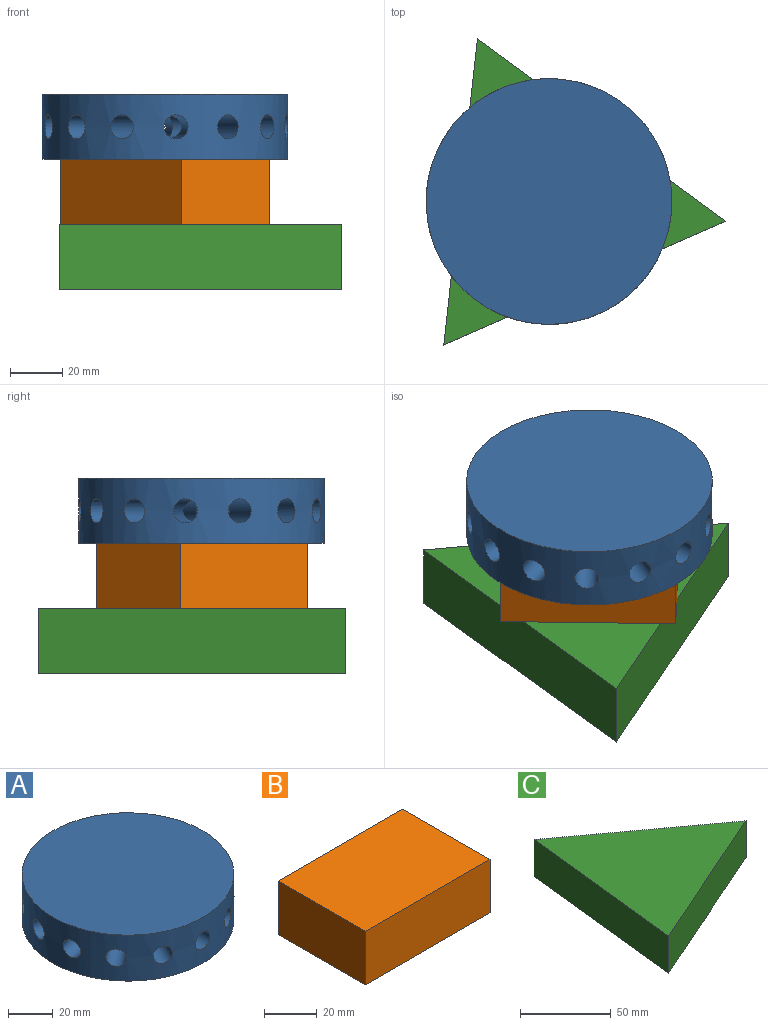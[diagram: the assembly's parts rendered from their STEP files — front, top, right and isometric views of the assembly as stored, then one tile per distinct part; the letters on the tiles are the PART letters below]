
ASSEMBLY  parts=3 mates=2
PART A: 17 faces, bbox 94.3x94.3x25 mm
  f0: cylinder r=47.14mm len=94.27mm, axis (0,0,-1), area 6466.9mm2, adj f1,f2,f3,f4,f5,f6,f7,f8
  f1: cylinder r=4.61mm len=48.01mm, axis (0.97,-0.22,0), area 989.8mm2, adj f0,f14,f15
  f2: cylinder r=4.61mm len=48.01mm, axis (0.97,-0.22,0), area 989.8mm2, adj f0,f13,f16
  f3: cylinder r=4.61mm len=46.47mm, axis (0.43,-0.9,0), area 989.8mm2, adj f0,f8,f16
  f4: cylinder r=4.61mm len=46.47mm, axis (0.43,-0.9,0), area 989.8mm2, adj f0,f7,f15
  f5: cylinder r=4.61mm len=42.6mm, axis (0.78,0.62,0), area 989.8mm2, adj f0,f12,f13
  f6: cylinder r=4.61mm len=42.6mm, axis (0.78,0.62,0), area 989.8mm2, adj f0,f11,f14
  f7: cylinder r=4.61mm len=47.14mm, axis (0,1,0), area 989.8mm2, adj f0,f4,f12
  f8: cylinder r=4.61mm len=47.14mm, axis (0,1,0), area 989.8mm2, adj f0,f3,f11
  f9: plane 94.27x94.27mm, normal (0,0,1), area 6979.8mm2, adj f0
  f10: plane 94.27x94.27mm, normal (0,0,-1), area 6979.8mm2, adj f0
  f11: cylinder r=4.61mm len=46.47mm, axis (-0.43,-0.9,0), area 989.8mm2, adj f0,f6,f8
  f12: cylinder r=4.61mm len=46.47mm, axis (-0.43,-0.9,0), area 989.8mm2, adj f0,f5,f7
  f13: cylinder r=4.61mm len=48.01mm, axis (-0.97,-0.22,0), area 989.8mm2, adj f0,f2,f5
  f14: cylinder r=4.61mm len=48.01mm, axis (-0.97,-0.22,0), area 989.8mm2, adj f0,f1,f6
  f15: cylinder r=4.61mm len=42.6mm, axis (-0.78,0.62,0), area 989.8mm2, adj f0,f1,f4
  f16: cylinder r=4.61mm len=42.6mm, axis (-0.78,0.62,0), area 989.8mm2, adj f0,f2,f3
PART B: 6 faces, bbox 67.2x47x25 mm
  f0: plane 67.23x25mm, normal (0,-1,0), area 1680.8mm2, adj f1,f3,f4,f5
  f1: plane 46.99x25mm, normal (1,0,0), area 1174.7mm2, adj f0,f2,f4,f5
  f2: plane 67.23x25mm, normal (0,1,0), area 1680.8mm2, adj f1,f3,f4,f5
  f3: plane 46.99x25mm, normal (-1,0,0), area 1174.7mm2, adj f0,f2,f4,f5
  f4: plane 67.23x46.99mm, normal (0,0,1), area 3159.2mm2, adj f0,f1,f2,f3
  f5: plane 67.23x46.99mm, normal (0,0,-1), area 3159.2mm2, adj f0,f1,f2,f3
PART C: 5 faces, bbox 108.2x117.5x25 mm
  f0: plane 117.47x25mm, normal (-0.99,0.11,0), area 2954.6mm2, adj f1,f2,f3,f4
  f1: plane 108.21x47.52mm, normal (0.4,-0.92,0), area 2954.6mm2, adj f0,f2,f3,f4
  f2: plane 95.26x69.96mm, normal (0.59,0.81,0), area 2954.6mm2, adj f0,f1,f3,f4
  f3: plane 117.47x108.21mm, normal (0,0,1), area 6048mm2, adj f0,f1,f2
  f4: plane 117.47x108.21mm, normal (0,0,-1), area 6048mm2, adj f0,f1,f2
PLACE A rot(axis=(-0.39,-0.92,0),180deg) t=(72.48,54.63,75)mm
PLACE B rot(axis=(0,0,1),133.8deg) t=(-70.7,73.8,25)mm
PLACE C t=(13.72,-71.19,0)mm
MATE revolute C.f3 <-> B.f5  axis (0,0,1) through (0,0,25)mm
MATE fastened B.f4 <-> A.f0  axis (0,0,1) through (0,0,50)mm
